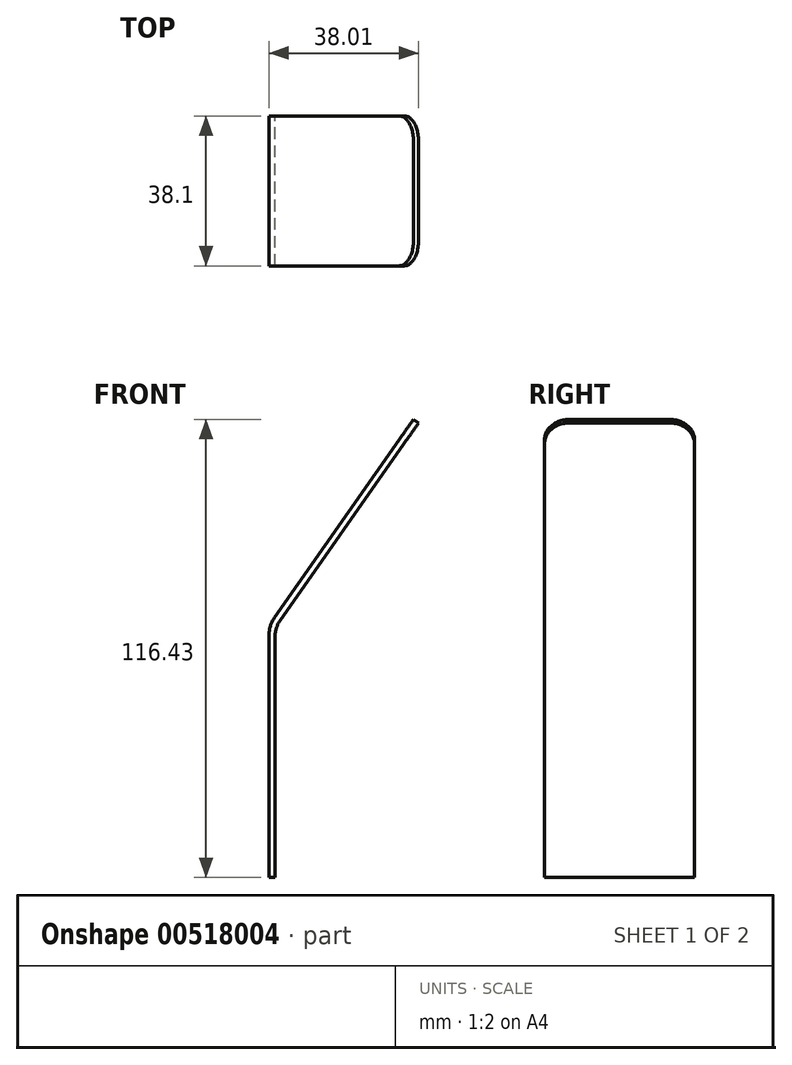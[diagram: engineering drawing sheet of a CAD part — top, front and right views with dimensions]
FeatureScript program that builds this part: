
annotation { "Feature Type Name" : "Feature", "Feature Type Description" : "" }
export const myFeature = defineFeature(function(context is Context, id is Id, definition is map)
    precondition{}
    {
        {
            var Q0;
            Q0=qCreatedBy(makeId("Front.planeOp"),FACE);
            var sketch = newSketch(context, id + "F0", { "sketchPlane" : qUnion([Q0])});
            skLineSegment(sketch, "E0", {"start": v(0, -2) * mm, "end": v(0, -63.5) * mm});
            skLineSegment(sketch, "E1", {"start": v(1.15, 1.64) * mm, "end": v(36.42, 52.02) * mm});
            skPoint(sketch, "E2.visualSharp", {"position": v(0, 0) * mm});
            skArc(sketch, "E2.filletArc", {"start": v(1.15, 1.64) * mm, "mid": v(0.3, -0.1) * mm, "end": v(0, -2) * mm});
            skLineSegment(sketch, "E3.0", {"start": v(-1.59, -2) * mm, "end": v(-1.59, -63.5) * mm});
            skArc(sketch, "E3.1", {"start": v(-0.15, 2.55) * mm, "mid": v(-1.22, 0.38) * mm, "end": v(-1.59, -2) * mm});
            skLineSegment(sketch, "E3.2", {"start": v(-0.15, 2.55) * mm, "end": v(35.12, 52.93) * mm});
            skLineSegment(sketch, "E4", {"start": v(35.12, 52.93) * mm, "end": v(36.42, 52.02) * mm});
            skLineSegment(sketch, "E5", {"start": v(-1.59, -63.5) * mm, "end": v(0, -63.5) * mm});
            skSolve(sketch);
        }
        {
            var Q0;
            Q0 = qSketchRegion(id + "F0", true);
            extrude(context, id + "F1", {"entities" : qUnion([Q0]), "depth" : (1.5) * 25.4 * mm, "offsetDistance" : 25 * mm});
        }
        {
            var Q0;
            Q0=makeQuery(id+"F1.opExtrude","CAP_EDGE",EDGE,{"disambiguationData":[OSD([sQuery(id+"F0.wireOp",EDGE,"E4")])],"isStart":false});
            var Q1;
            Q1=makeQuery(id+"F1.opExtrude","CAP_EDGE",EDGE,{"disambiguationData":[OSD([sQuery(id+"F0.wireOp",EDGE,"E4")])],"isStart":true});
            fillet(context, id + "F2", {"entities" : qUnion([Q0, Q1]), "radius" : 6.35 * mm, "tangentPropagation" : true, "allowEdgeOverflow" : false});
        }
    });
